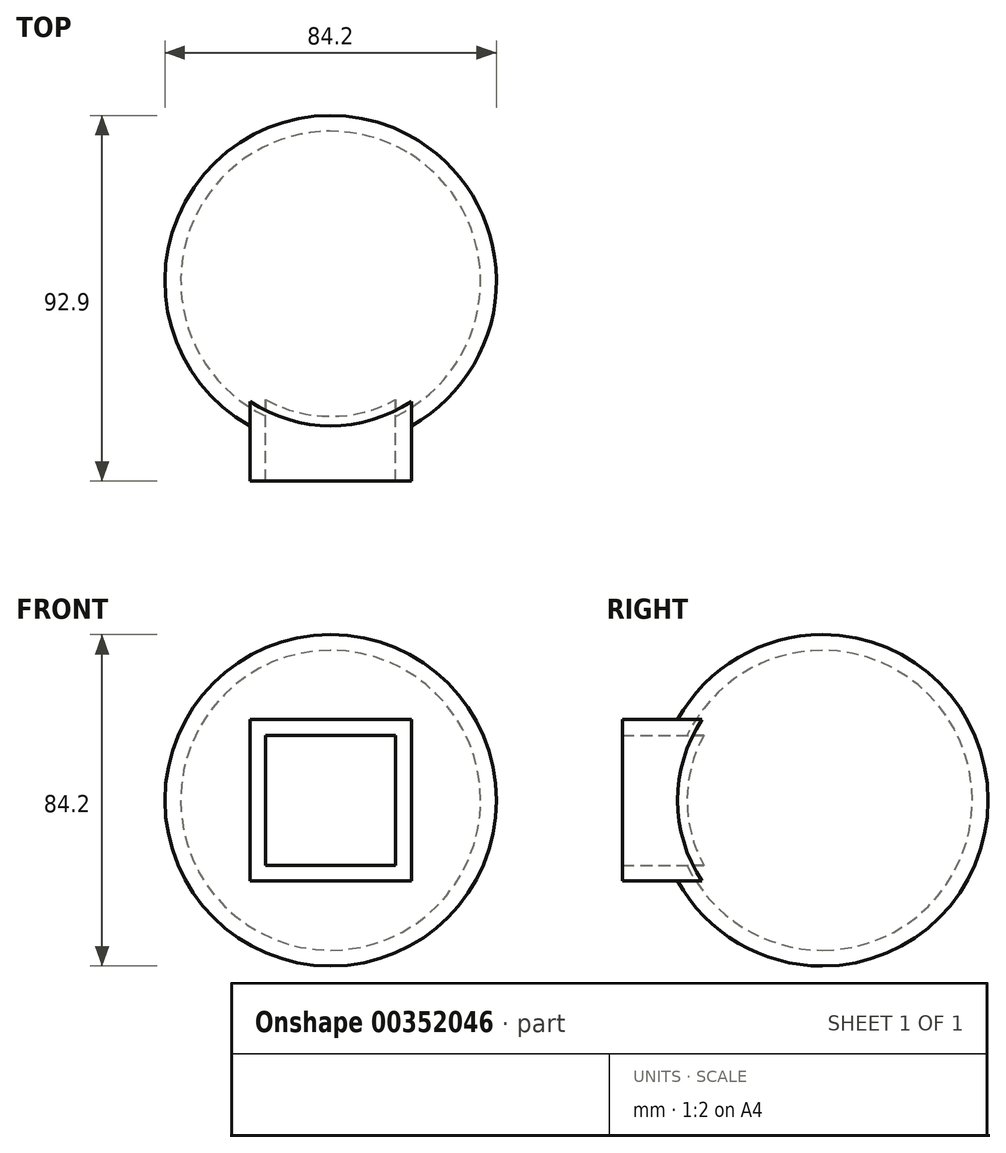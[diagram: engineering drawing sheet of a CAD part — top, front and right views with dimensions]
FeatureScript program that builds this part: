
annotation { "Feature Type Name" : "Feature", "Feature Type Description" : "" }
export const myFeature = defineFeature(function(context is Context, id is Id, definition is map)
    precondition{}
    {
        {
            var Q0;
            Q0=qCreatedBy(makeId("Front.planeOp"),FACE);
            var sketch = newSketch(context, id + "F0", { "sketchPlane" : qUnion([Q0])});
            skCircle(sketch, "E0", {"center": v(0, 0) * mm, "radius": 38.1 * mm});
            skLineSegment(sketch, "E1", {"start": v(0, 38.1) * mm, "end": v(0, -38.1) * mm});
            skSolve(sketch);
        }
        {
            var Q0;
            {var subQ0=sQuery(id+"F0.wireOp",EDGE,"E1");Q0=makeQuery(id+"F0.imprint","IMPRINT",FACE,{"disambiguationData":[TD([[makeQuery(id+"F0.imprint","IMPRINT",EDGE,{"derivedFrom":subQ0}),1.0]])]});}
            var Q1;
            Q1=sQuery(id+"F0.wireOp",EDGE,"E1");
            revolve(context, id + "F1", {"entities" : qUnion([Q0]), "axis" : qUnion([Q1]), "revolveType" : RevolveType.FULL});
        }
        {
            var Q0;
            Q0=qCreatedBy(makeId("Front.planeOp"),FACE);
            cPlane(context, id + "F2", {"entities" : qUnion([Q0]), "cplaneType" : CPlaneType.OFFSET, "offset" : 25.4 * mm, "width" : 152.4 * mm, "height" : 152.4 * mm});
        }
        {
            var Q0;
            Q0=qCreatedBy(id+"F2.planeOp",FACE);
            var sketch = newSketch(context, id + "F3", { "sketchPlane" : qUnion([Q0])});
            skLineSegment(sketch, "E2.bottom", {"start": v(16.51, 16.51) * mm, "end": v(-16.51, 16.51) * mm});
            skLineSegment(sketch, "E2.top", {"start": v(16.51, -16.51) * mm, "end": v(-16.51, -16.51) * mm});
            skLineSegment(sketch, "E2.left", {"start": v(16.51, 16.51) * mm, "end": v(16.51, -16.51) * mm});
            skLineSegment(sketch, "E2.right", {"start": v(-16.51, 16.51) * mm, "end": v(-16.51, -16.51) * mm});
            skPoint(sketch, "E2.middle", {"position": v(0, 0) * mm});
            skSolve(sketch);
        }
        {
            var Q0;
            Q0 = qSketchRegion(id + "F3", true);
            extrude(context, id + "F4", {"entities" : qUnion([Q0]), "operationType" : NewBodyOperationType.ADD, "depth" : 25.4 * mm});
        }
        {
            var Q0;
            Q0=makeQuery(id+"F4.opExtrude","CAP_FACE",FACE,{"disambiguationData":[OSD([sQuery(id+"F3.wireOp",EDGE,"E2.bottom"),sQuery(id+"F3.wireOp",EDGE,"E2.top"),sQuery(id+"F3.wireOp",EDGE,"E2.left"),sQuery(id+"F3.wireOp",EDGE,"E2.right")])],"isStart":false});
            shell(context, id + "F5", {"entities" : qUnion([Q0]), "thickness" : 4 * mm, "oppositeDirection" : true});
        }
    });
